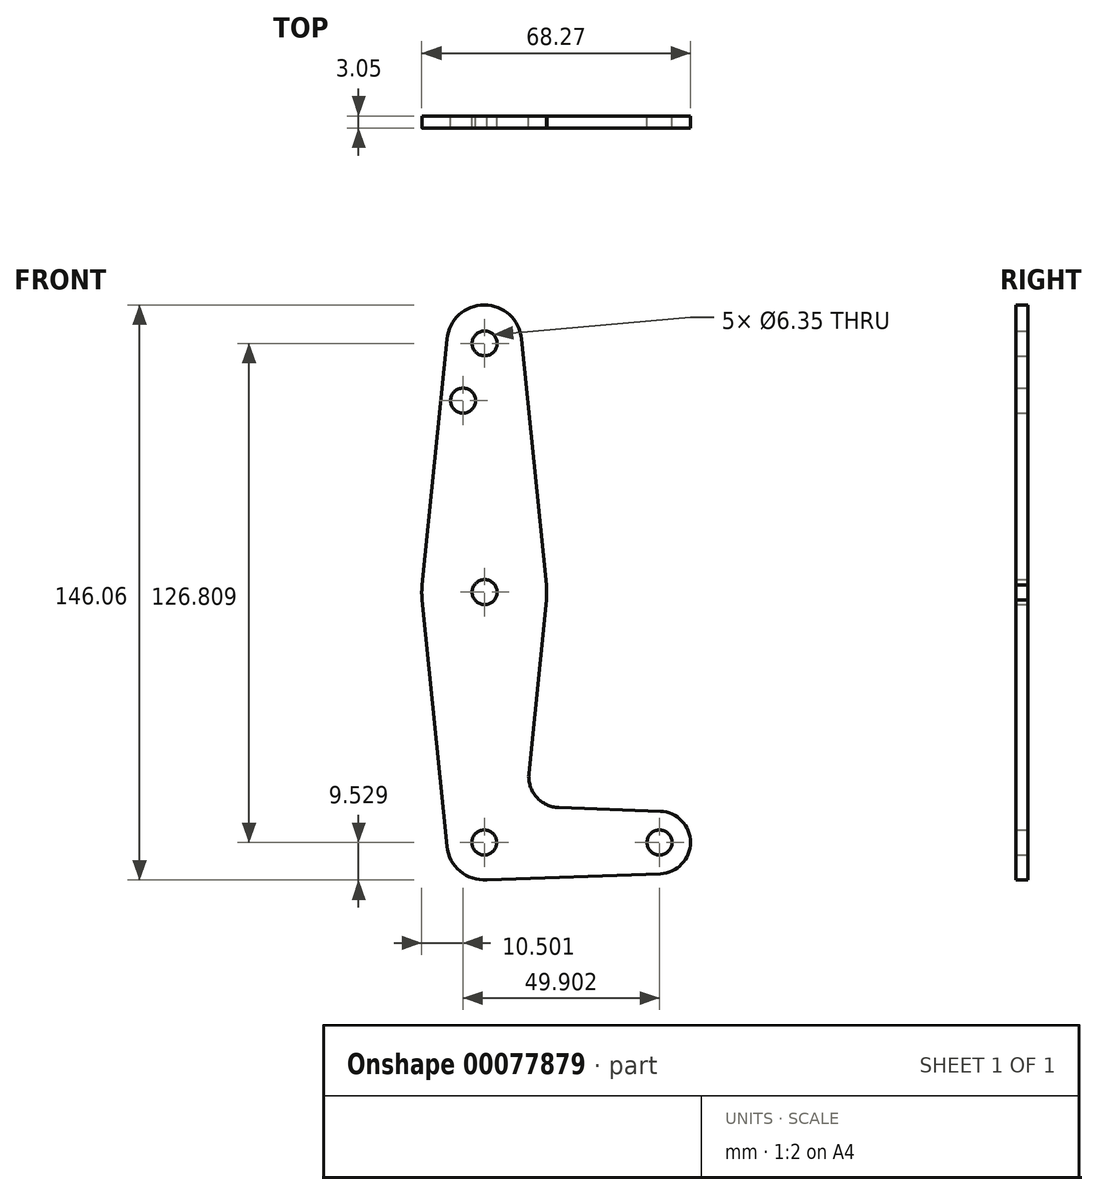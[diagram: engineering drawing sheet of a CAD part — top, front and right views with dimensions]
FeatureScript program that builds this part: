
annotation { "Feature Type Name" : "Feature", "Feature Type Description" : "" }
export const myFeature = defineFeature(function(context is Context, id is Id, definition is map)
    precondition{}
    {
        {
            var Q0;
            Q0=qCreatedBy(makeId("Front.planeOp"),FACE);
            var sketch = newSketch(context, id + "F0", { "sketchPlane" : qUnion([Q0])});
            skCircle(sketch, "E0", {"center": v(0, 0) * mm, "radius": 9.53 * mm});
            skLineSegment(sketch, "E1", {"start": v(0, 0) * mm, "end": v(0, 63.5) * mm, "construction": true});
            skCircle(sketch, "E2", {"center": v(0, 63.5) * mm, "radius": 15.88 * mm});
            skLineSegment(sketch, "E3", {"start": v(0, 63.5) * mm, "end": v(0, 127) * mm, "construction": true});
            skLineSegment(sketch, "E4", {"start": v(0, 0) * mm, "end": v(44.45, 0) * mm, "construction": true});
            skCircle(sketch, "E5", {"center": v(0, 127) * mm, "radius": 9.53 * mm});
            skCircle(sketch, "E6", {"center": v(44.45, 0) * mm, "radius": 7.94 * mm});
            skCircle(sketch, "E7", {"center": v(0, 0) * mm, "radius": 3.18 * mm});
            skLineSegment(sketch, "E8", {"start": v(-15.82, 64.77) * mm, "end": v(-9.48, 127.95) * mm});
            skLineSegment(sketch, "E9", {"start": v(15.82, 64.77) * mm, "end": v(9.48, 127.95) * mm});
            skLineSegment(sketch, "E10", {"start": v(-15.82, 62.23) * mm, "end": v(-9.48, -0.95) * mm});
            skLineSegment(sketch, "E11", {"start": v(15.82, 62.23) * mm, "end": v(11.34, 17.59) * mm});
            skLineSegment(sketch, "E12", {"start": v(0, -9.53) * mm, "end": v(44.73, -7.93) * mm});
            skLineSegment(sketch, "E13", {"start": v(18.97, 8.85) * mm, "end": v(44.73, 7.93) * mm});
            skArc(sketch, "E14.filletArc", {"start": v(11.34, 17.59) * mm, "mid": v(13.26, 11.57) * mm, "end": v(18.97, 8.85) * mm});
            skCircle(sketch, "E15", {"center": v(44.52, 0) * mm, "radius": 3.18 * mm});
            skCircle(sketch, "E16", {"center": v(0.1, 63.6) * mm, "radius": 3.18 * mm});
            skCircle(sketch, "E17", {"center": v(0.1, 126.8) * mm, "radius": 3.18 * mm});
            skCircle(sketch, "E18", {"center": v(-5.38, 112.27) * mm, "radius": 3.18 * mm});
            skSolve(sketch);
        }
        {
            var Q0;
            Q0 = qSketchRegion(id + "F0", true);
            extrude(context, id + "F1", {"entities" : qUnion([Q0]), "depth" : 3.05 * mm});
        }
    });
